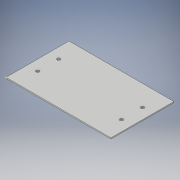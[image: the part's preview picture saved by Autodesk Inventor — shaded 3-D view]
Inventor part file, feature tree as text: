
AUTODESK INVENTOR PART (.ipt)
format: ipt  version: 2019 (Build 230136000, 136)  size: 107,008 bytes
history: native  units: mm
features: sketch x6, extrude x3
ambient origin geometry x8: Origin, YZ Plane, XZ Plane, XY Plane, X Axis, Y Axis, Z Axis, Center Point
bodies: Solid1 (feature_tree)
feature tree (9):
  extrude  "Extrusion1"  Depth=60.0mm
  extrude  "Extrusion3"  Depth=1.0mm
  sketch  "Sketch4"  dims[d12=3.0mm d13=1.0mm d14=0.0mm]
  sketch  "Sketch5"  dims[d15=3.0mm]
  sketch  "Sketch6"  dims[d16=3.0mm]
  extrude  "Extrusion4"  Depth=1.0mm TaperAngle=0.0deg
  sketch  "Sketch1"  dims[d2=100.0mm d3=60.0mm]
  sketch  "Sketch3"  dims[d4=1.0mm d5=0.0mm d11=3.0mm]
  sketch  "Sketch7"  dims[d17=1.0mm d18=0.0mm]
